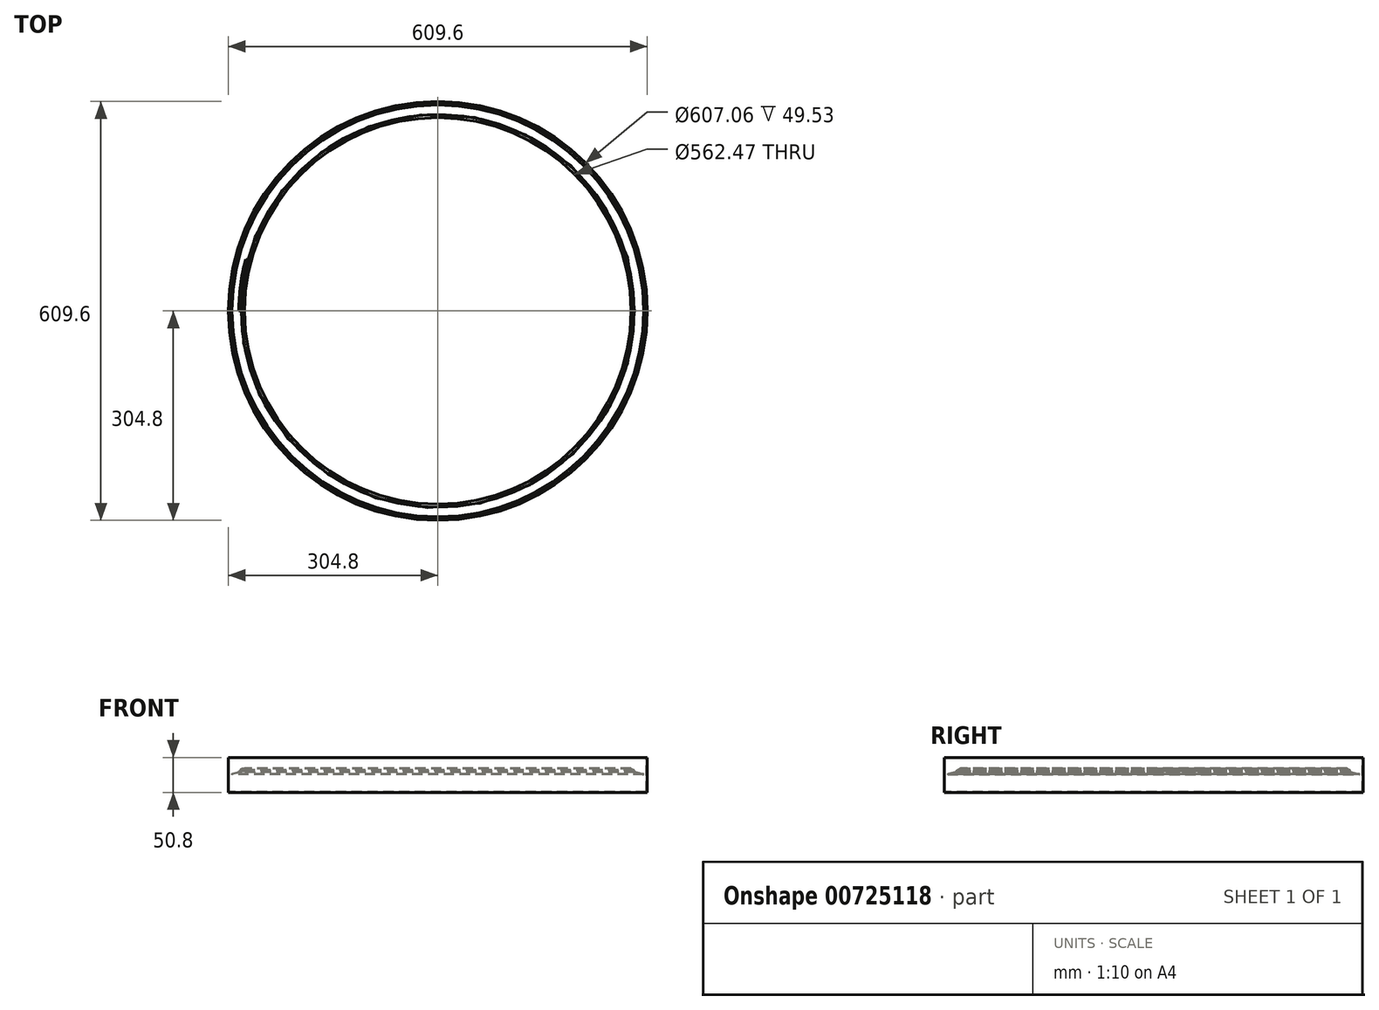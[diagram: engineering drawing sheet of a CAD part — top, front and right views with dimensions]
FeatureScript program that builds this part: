
annotation { "Feature Type Name" : "Feature", "Feature Type Description" : "" }
export const myFeature = defineFeature(function(context is Context, id is Id, definition is map)
    precondition{}
    {
        {
            var Q0;
            Q0=qCreatedBy(makeId("Front.planeOp"),FACE);
            var sketch = newSketch(context, id + "F0", { "sketchPlane" : qUnion([Q0])});
            skLineSegment(sketch, "E0.left", {"start": v(-304.8, -3.12) * mm, "end": v(-304.8, -28.52) * mm});
            skLineSegment(sketch, "E1", {"start": v(-287.1, 1.63) * mm, "end": v(-299.7, -1.75) * mm});
            skLineSegment(sketch, "E2", {"start": v(-286.3, 0.52) * mm, "end": v(-299.7, -3.07) * mm});
            skPoint(sketch, "E3.orphan", {"position": v(-304.8, 0) * mm});
            skLineSegment(sketch, "E4", {"start": v(-304.8, -3.12) * mm, "end": v(-304.8, 22.28) * mm});
            skLineSegment(sketch, "E5", {"start": v(-304.8, 22.28) * mm, "end": v(-303.53, 22.28) * mm});
            skLineSegment(sketch, "E6", {"start": v(-303.53, 22.28) * mm, "end": v(-303.53, -2.78) * mm});
            skLineSegment(sketch, "E7", {"start": v(-304.8, -28.52) * mm, "end": v(0, -28.52) * mm});
            skLineSegment(sketch, "E8", {"start": v(-303.53, -27.25) * mm, "end": v(-303.53, -4.1) * mm});
            skLineSegment(sketch, "E9", {"start": v(-303.53, -27.25) * mm, "end": v(0, -27.25) * mm});
            skLineSegment(sketch, "E10", {"start": v(0, -28.52) * mm, "end": v(0, -27.25) * mm});
            skLineSegment(sketch, "E11", {"start": v(-286.55, 2.56) * mm, "end": v(-286.55, 2.56) * mm});
            skPoint(sketch, "E12.visualSharp", {"position": v(-286.85, 3.66) * mm});
            skArc(sketch, "E12.filletArc", {"start": v(-285.74, 3.96) * mm, "mid": v(-286.44, 3.43) * mm, "end": v(-286.55, 2.56) * mm});
            skPoint(sketch, "E13.newPointA", {"position": v(-286.36, 1.82) * mm});
            skArc(sketch, "E13.filletArc", {"start": v(-287.1, 1.63) * mm, "mid": v(-286.63, 1.98) * mm, "end": v(-286.55, 2.56) * mm});
            skLineSegment(sketch, "E14", {"start": v(-299.7, -1.75) * mm, "end": v(-299.7, -3.07) * mm});
            skLineSegment(sketch, "E15", {"start": v(-303.53, -2.78) * mm, "end": v(-303.53, -4.1) * mm});
            skLineSegment(sketch, "E16.0", {"start": v(-287.44, 2.45) * mm, "end": v(-289.36, 1.94) * mm});
            skArc(sketch, "E16.1", {"start": v(-285.97, 4.82) * mm, "mid": v(-287.18, 3.93) * mm, "end": v(-287.44, 2.45) * mm});
            skArc(sketch, "E17.1", {"start": v(-286.14, 5.43) * mm, "mid": v(-287.54, 4.5) * mm, "end": v(-288.11, 2.93) * mm});
            skLineSegment(sketch, "E17.2", {"start": v(-288.11, 2.93) * mm, "end": v(-289.53, 2.55) * mm});
            skLineSegment(sketch, "E18", {"start": v(-289.36, 1.94) * mm, "end": v(-289.53, 2.55) * mm});
            skPoint(sketch, "E19.start.orphan", {"position": v(-275.8, 6.62) * mm});
            skLineSegment(sketch, "E20", {"start": v(-285.74, 3.96) * mm, "end": v(-281.24, 6.47) * mm});
            skLineSegment(sketch, "E21", {"start": v(-284.86, 5.45) * mm, "end": v(-285.97, 4.82) * mm});
            skLineSegment(sketch, "E22", {"start": v(-286.14, 5.43) * mm, "end": v(-285.16, 5.98) * mm});
            skLineSegment(sketch, "E23", {"start": v(-281.24, 6.47) * mm, "end": v(-281.24, 5.2) * mm});
            skLineSegment(sketch, "E24", {"start": v(-281.24, 5.2) * mm, "end": v(-285.54, 3.34) * mm});
            skLineSegment(sketch, "E25", {"start": v(-285.54, 3.34) * mm, "end": v(-286.16, 2.6) * mm});
            skLineSegment(sketch, "E26", {"start": v(-286.16, 2.6) * mm, "end": v(-286.3, 0.52) * mm});
            skLineSegment(sketch, "E27", {"start": v(-285.16, 5.98) * mm, "end": v(-284.86, 5.45) * mm});
            skSolve(sketch);
        }
        {
            var Q0;
            Q0=qCreatedBy(makeId("Front.planeOp"),FACE);
            var sketch = newSketch(context, id + "F1", { "sketchPlane" : qUnion([Q0])});
            skLineSegment(sketch, "E28", {"start": v(0, 40.5) * mm, "end": v(0, -62.38) * mm});
            skSolve(sketch);
        }
        {
            var Q0;
            Q0=makeQuery(id+"F0.imprint","IMPRINT",FACE,{"disambiguationData":[TD([[makeQuery(id+"F0.imprint","IMPRINT",EDGE,{"derivedFrom":sQuery(id+"F0.wireOp",EDGE,"E0.left")}),1.0]])]});
            var Q1;
            Q1=sQuery(id+"F1.wireOp",EDGE,"E28");
            revolve(context, id + "F2", {"surfaceOperationType" : NewSurfaceOperationType.NEW, "entities" : qUnion([Q0]), "axis" : qUnion([Q1]), "revolveType" : RevolveType.FULL});
        }
        {
            var Q0;
            Q0=makeQuery(id+"F0.imprint","IMPRINT",FACE,{"disambiguationData":[TD([[makeQuery(id+"F0.imprint","IMPRINT",EDGE,{"derivedFrom":sQuery(id+"F0.wireOp",EDGE,"E1")}),1.0]])]});
            var Q1;
            Q1=sQuery(id+"F1.wireOp",EDGE,"E28");
            revolve(context, id + "F3", {"surfaceOperationType" : NewSurfaceOperationType.NEW, "entities" : qUnion([Q0]), "axis" : qUnion([Q1]), "revolveType" : RevolveType.FULL});
        }
        {
            var Q0;
            Q0=makeQuery(id+"F0.imprint","IMPRINT",FACE,{"disambiguationData":[TD([[makeQuery(id+"F0.imprint","IMPRINT",EDGE,{"derivedFrom":sQuery(id+"F0.wireOp",EDGE,"E16.0")}),-1.0]])]});
            var Q1;
            Q1=sQuery(id+"F1.wireOp",EDGE,"E28");
            revolve(context, id + "F4", {"surfaceOperationType" : NewSurfaceOperationType.NEW, "entities" : qUnion([Q0]), "axis" : qUnion([Q1]), "revolveType" : RevolveType.ONE_DIRECTION, "angle" : 15 * degree});
        }
    });
